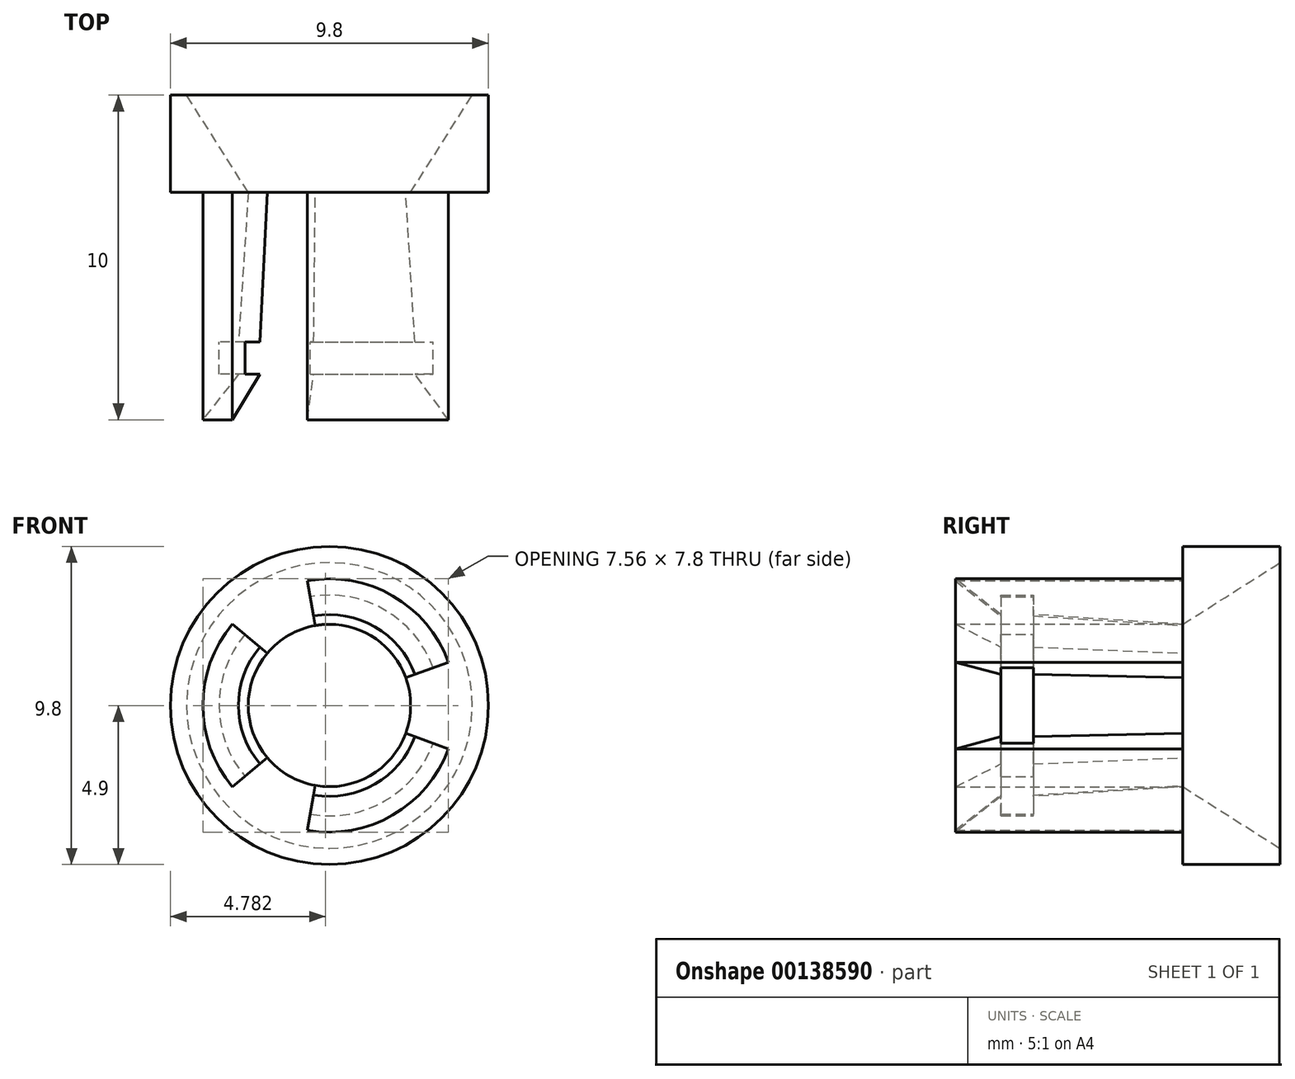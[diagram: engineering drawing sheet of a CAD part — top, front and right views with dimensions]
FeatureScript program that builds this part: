
annotation { "Feature Type Name" : "Feature", "Feature Type Description" : "" }
export const myFeature = defineFeature(function(context is Context, id is Id, definition is map)
    precondition{}
    {
        {
            var Q0;
            Q0=qCreatedBy(makeId("Right.planeOp"),FACE);
            var sketch = newSketch(context, id + "F0", { "sketchPlane" : qUnion([Q0])});
            skLineSegment(sketch, "E0", {"start": v(-3, 2.5) * mm, "end": v(-7.6, 2.8) * mm});
            skLineSegment(sketch, "E1", {"start": v(-7.6, 2.8) * mm, "end": v(-7.6, 3.4) * mm});
            skLineSegment(sketch, "E2", {"start": v(-7.6, 3.4) * mm, "end": v(-8.6, 3.4) * mm});
            skLineSegment(sketch, "E3", {"start": v(-8.6, 3.4) * mm, "end": v(-8.6, 2.8) * mm});
            skLineSegment(sketch, "E4", {"start": v(-10, 3.9) * mm, "end": v(-8.6, 2.8) * mm});
            skLineSegment(sketch, "E5", {"start": v(0, 0) * mm, "end": v(-13.95, 0) * mm, "construction": true});
            skLineSegment(sketch, "E6", {"start": v(-3, 3.9) * mm, "end": v(-3, 4.9) * mm});
            skLineSegment(sketch, "E7", {"start": v(-3, 4.9) * mm, "end": v(0, 4.9) * mm});
            skLineSegment(sketch, "E8", {"start": v(-10, 3.9) * mm, "end": v(-3, 3.9) * mm});
            skLineSegment(sketch, "E9", {"start": v(0, 4.9) * mm, "end": v(0, 4.4) * mm});
            skLineSegment(sketch, "E10", {"start": v(0, 4.4) * mm, "end": v(-3, 2.5) * mm});
            skSolve(sketch);
        }
        {
            var Q0;
            Q0=makeQuery(id+"F0.imprint","IMPRINT",FACE,{"disambiguationData":[TD([[makeQuery(id+"F0.imprint","IMPRINT",EDGE,{"derivedFrom":sQuery(id+"F0.wireOp",EDGE,"E0")}),-1.0]])]});
            var Q1;
            Q1=sQuery(id+"F0.wireOp",EDGE,"E5");
            revolve(context, id + "F1", {"entities" : qUnion([Q0]), "axis" : qUnion([Q1]), "revolveType" : RevolveType.FULL});
        }
        {
            var Q0;
            Q0=makeQuery(id+"F1.opRevolve","SWEPT_FACE",FACE,{"disambiguationData":[OSD([sQuery(id+"F0.wireOp",EDGE,"E6")])]});
            var sketch = newSketch(context, id + "F2", { "sketchPlane" : qUnion([Q0])});
            skLineSegment(sketch, "E11", {"start": v(0, 0) * mm, "end": v(-0.96, 5.47) * mm});
            skCircle(sketch, "E12", {"center": v(0, 0) * mm, "radius": 5.55 * mm});
            skLineSegment(sketch, "E13", {"start": v(0, 0) * mm, "end": v(5.55, 0) * mm});
            skLineSegment(sketch, "E14", {"start": v(0, 0) * mm, "end": v(-0.96, -5.47) * mm});
            skLineSegment(sketch, "E15", {"start": v(0, 0) * mm, "end": v(-4.25, 3.57) * mm});
            skLineSegment(sketch, "E16", {"start": v(0, 0) * mm, "end": v(5.22, -1.9) * mm});
            skLineSegment(sketch, "E17", {"start": v(0, 0) * mm, "end": v(-4.25, -3.57) * mm});
            skLineSegment(sketch, "E18", {"start": v(0, 0) * mm, "end": v(5.22, 1.9) * mm});
            skSolve(sketch);
        }
        {
            var Q0;
            {var subQ1=sQuery(id+"F2.wireOp",EDGE,"E11");var subQ3=makeQuery(id+"F1.opRevolve","SWEPT_EDGE",EDGE,{"disambiguationData":[OSD([sQuery(id+"F0.wireOp",EDGE,"E6"),sQuery(id+"F0.wireOp",EDGE,"E8")])]});var subQ4=makeQuery(id+"F2.imprint","INTERSECT",VERTEX,{"derivedFrom":[subQ3,subQ1]});Q0=makeQuery(id+"F2.imprint","IMPRINT",FACE,{"disambiguationData":[TD([[makeQuery(id+"F2.imprint","IMPRINT",EDGE,{"disambiguationData":[TD([[subQ4,1.0]])],"derivedFrom":subQ3}),-1.0]])]});}
            var Q1;
            {var subQ1=sQuery(id+"F2.wireOp",EDGE,"E14");var subQ3=makeQuery(id+"F1.opRevolve","SWEPT_EDGE",EDGE,{"disambiguationData":[OSD([sQuery(id+"F0.wireOp",EDGE,"E6"),sQuery(id+"F0.wireOp",EDGE,"E8")])]});var subQ4=makeQuery(id+"F2.imprint","INTERSECT",VERTEX,{"derivedFrom":[subQ3,subQ1]});Q1=makeQuery(id+"F2.imprint","IMPRINT",FACE,{"disambiguationData":[TD([[makeQuery(id+"F2.imprint","IMPRINT",EDGE,{"disambiguationData":[TD([[subQ4,-1.0]])],"derivedFrom":subQ3}),-1.0]])]});}
            var Q2;
            {var subQ1=sQuery(id+"F2.wireOp",EDGE,"E13");var subQ3=makeQuery(id+"F1.opRevolve","SWEPT_EDGE",EDGE,{"disambiguationData":[OSD([sQuery(id+"F0.wireOp",EDGE,"E6"),sQuery(id+"F0.wireOp",EDGE,"E8")])]});var subQ4=makeQuery(id+"F2.imprint","INTERSECT",VERTEX,{"derivedFrom":[subQ3,subQ1]});Q2=makeQuery(id+"F2.imprint","IMPRINT",FACE,{"disambiguationData":[TD([[makeQuery(id+"F2.imprint","IMPRINT",EDGE,{"disambiguationData":[TD([[subQ4,-1.0]])],"derivedFrom":subQ3}),-1.0]])]});}
            var Q3;
            {var subQ1=sQuery(id+"F2.wireOp",EDGE,"E13");var subQ3=makeQuery(id+"F1.opRevolve","SWEPT_EDGE",EDGE,{"disambiguationData":[OSD([sQuery(id+"F0.wireOp",EDGE,"E6"),sQuery(id+"F0.wireOp",EDGE,"E8")])]});var subQ4=makeQuery(id+"F2.imprint","INTERSECT",VERTEX,{"derivedFrom":[subQ3,subQ1]});Q3=makeQuery(id+"F2.imprint","IMPRINT",FACE,{"disambiguationData":[TD([[makeQuery(id+"F2.imprint","IMPRINT",EDGE,{"disambiguationData":[TD([[subQ4,1.0]])],"derivedFrom":subQ3}),-1.0]])]});}
            extrude(context, id + "F3", {"entities" : qUnion([Q0, Q1, Q2, Q3]), "operationType" : NewBodyOperationType.REMOVE, "depth" : 10 * mm});
        }
    });
